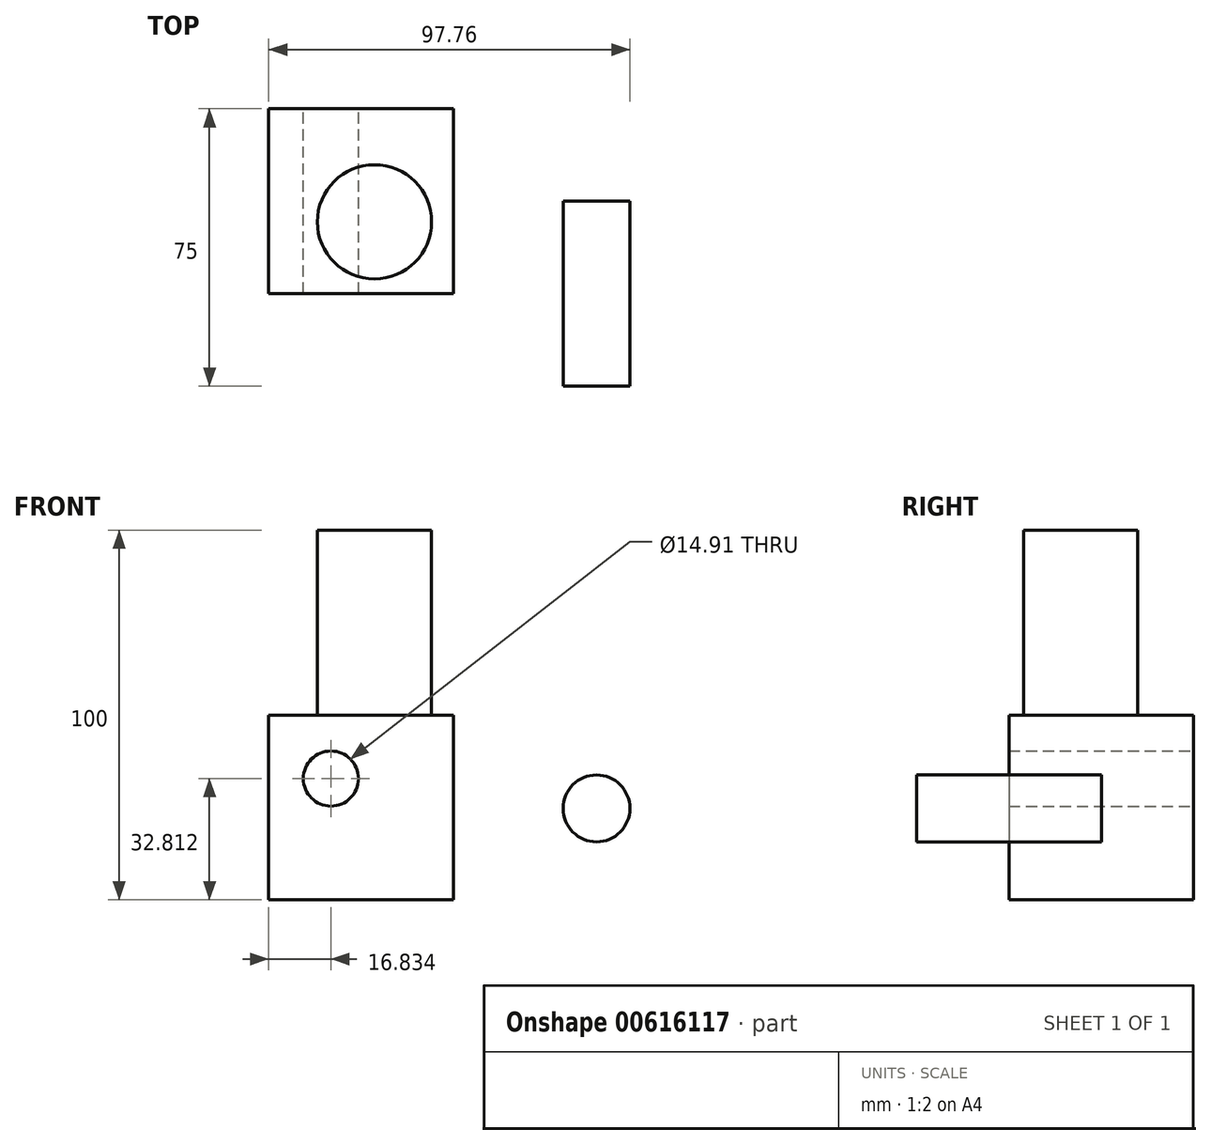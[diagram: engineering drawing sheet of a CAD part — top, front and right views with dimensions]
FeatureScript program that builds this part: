
annotation { "Feature Type Name" : "Feature", "Feature Type Description" : "" }
export const myFeature = defineFeature(function(context is Context, id is Id, definition is map)
    precondition{}
    {
        {
            var Q0;
            Q0=qCreatedBy(makeId("Top.planeOp"),FACE);
            var sketch = newSketch(context, id + "F0", { "sketchPlane" : qUnion([Q0])});
            skLineSegment(sketch, "E0.bottom", {"start": v(-27.48, -25) * mm, "end": v(22.52, -25) * mm});
            skLineSegment(sketch, "E0.top", {"start": v(-27.48, 25) * mm, "end": v(22.52, 25) * mm});
            skLineSegment(sketch, "E0.left", {"start": v(-27.48, -25) * mm, "end": v(-27.48, 25) * mm});
            skLineSegment(sketch, "E0.right", {"start": v(22.52, -25) * mm, "end": v(22.52, 25) * mm});
            skPoint(sketch, "E0.middle", {"position": v(-2.48, 0) * mm});
            skSolve(sketch);
        }
        {
            var Q0;
            Q0 = qSketchRegion(id + "F0", true);
            extrude(context, id + "F1", {"entities" : qUnion([Q0]), "depth" : 50 * mm, "offsetDistance" : 25 * mm});
        }
        {
            var Q0;
            Q0=qCreatedBy(makeId("Front.planeOp"),FACE);
            var sketch = newSketch(context, id + "F2", { "sketchPlane" : qUnion([Q0])});
            skCircle(sketch, "E1", {"center": v(61.23, 24.75) * mm, "radius": 9.05 * mm});
            skSolve(sketch);
        }
        {
            var Q0;
            Q0=makeQuery(id+"F2.imprint","IMPRINT",FACE,{"disambiguationData":[TD([[makeQuery(id+"F2.imprint","IMPRINT",EDGE,{"derivedFrom":sQuery(id+"F2.wireOp",EDGE,"E1")}),1.0]])]});
            extrude(context, id + "F3", {"entities" : qUnion([Q0]), "depth" : 50 * mm, "offsetDistance" : 25 * mm});
        }
        {
            var Q0;
            Q0=makeQuery(id+"F1.opExtrude","CAP_FACE",FACE,{"disambiguationData":[OSD([sQuery(id+"F0.wireOp",EDGE,"E0.bottom"),sQuery(id+"F0.wireOp",EDGE,"E0.top"),sQuery(id+"F0.wireOp",EDGE,"E0.left"),sQuery(id+"F0.wireOp",EDGE,"E0.right")])],"isStart":false});
            var sketch = newSketch(context, id + "F4", { "sketchPlane" : qUnion([Q0])});
            skCircle(sketch, "E2", {"center": v(1.14, -5.6) * mm, "radius": 15.45 * mm});
            skPoint(sketch, "E2.first.point", {"position": v(-3.35, 9.19) * mm});
            skPoint(sketch, "E2.second.point", {"position": v(11.81, -16.77) * mm});
            skPoint(sketch, "E2.third.point", {"position": v(-14.15, -3.35) * mm});
            skSolve(sketch);
        }
        {
            var Q0;
            Q0=makeQuery(id+"F1.opExtrude","SWEPT_FACE",FACE,{"disambiguationData":[OSD([sQuery(id+"F0.wireOp",EDGE,"E0.top")])]});
            var sketch = newSketch(context, id + "F5", { "sketchPlane" : qUnion([Q0])});
            skCircle(sketch, "E3", {"center": v(10.65, 32.81) * mm, "radius": 7.45 * mm});
            skSolve(sketch);
        }
        {
            var Q0;
            Q0 = qSketchRegion(id + "F5", true);
            var Q1;
            Q1=sQuery(id+"F5.wireOp",EDGE,"E3");
            extrude(context, id + "F6", {"entities" : qUnion([Q0]), "operationType" : NewBodyOperationType.REMOVE, "surfaceEntities" : qUnion([Q1]), "oppositeDirection" : true, "depth" : 60 * mm, "offsetDistance" : 25 * mm});
        }
        {
            var Q0;
            Q0=makeQuery(id+"F4.imprint","IMPRINT",FACE,{"disambiguationData":[TD([[makeQuery(id+"F4.imprint","IMPRINT",EDGE,{"derivedFrom":sQuery(id+"F4.wireOp",EDGE,"E2")}),1.0]])]});
            extrude(context, id + "F7", {"entities" : qUnion([Q0]), "operationType" : NewBodyOperationType.ADD, "depth" : 50 * mm, "offsetDistance" : 25 * mm});
        }
    });
